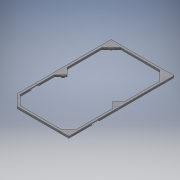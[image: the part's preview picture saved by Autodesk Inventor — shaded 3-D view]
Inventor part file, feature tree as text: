
AUTODESK INVENTOR PART (.ipt)
format: ipt  version: 2016 SP2 (Build 200236200, 236)  size: 166,912 bytes
history: native  units: mm
features: reference x15, extrude x3, sketch x3
ambient origin geometry x8: Origin, YZ Plane, XZ Plane, XY Plane, X Axis, Y Axis, Z Axis, Center Point
bodies: Volumenkörper1 (feature_tree)
feature tree (21):
  extrude  "Extrusion1"  Depth=3.0mm
  extrude  "Extrusion2"  Depth=3.0mm
  extrude  "Extrusion3"  TaperAngle=45.0deg  [1 undecoded]
  sketch  "Skizze1"  dims[d0=3.0mm d1=3.0mm]
  reference  "Referenz1"
  reference  "Referenz2"
  reference  "Referenz3"
  reference  "Referenz4"
  reference  "Referenz5"
  reference  "Referenz6"
  reference  "Referenz7"
  reference  "Referenz8"
  reference  "Referenz9"
  reference  "Referenz10"
  sketch  "Skizze2"  dims[d2=3.0mm d3=3.0mm]
  reference  "Referenz11"
  reference  "Referenz12"
  reference  "Referenz13"
  reference  "Referenz14"
  reference  "Referenz15"
  sketch  "Skizze3"  dims[d4=5.0mm d5=45.0deg d6=5.0mm d7=45.0deg d8=4.0mm d9=4.0mm d10=4.0mm d11=4.0mm d12=5.0mm d13=3.0mm d14=15.0mm d15=2.5mm d16=0.0mm d17=2.5mm d18=0.0mm d19=10.0mm d20=15.0mm d21=10.0mm d22=4.0mm d23=1.5mm d24=0.0mm]
note: 1 required parameter value undecoded (feature->parameter linkage not recoverable at this tier; creation-order binding heuristic only, values carry confidence <= 0.55)
